# Revit family: Incepa_Zip_Acabamento Registro Base Reforma_1.2-3.4-1
name_source: partatom
category: Plumbing Fixtures
revit_build: Autodesk Revit Architecture 2014 (Build: 20131024_2115(x64)
units: mm (PartAtom-declared; Revit-internal decimal feet)

## types (1)
- Para base reforma 1/2", 3/4" e 1"
    Assembly Code = D2010
    CW Connection = No
    CWFU = 0
    Cost = 0 $
    Default Elevation = 1200 mm
    Description = Acabamento de registro para base reforma 1/2", 3/4" e 1" (B5009I9CR3), linha Incepa One - Metais Incepa
    Desenvolvido por = ofcdesk
    HW Connection = No
    HWFU = 0
    Incepa: Categoria = Lavatório
    Incepa: Cores Disponíveis = Cromado
    Incepa: Código = B5009I9CR3
    Incepa: Descrição = Acabamento de registro para base reforma 1/2", 3/4" e 1" (B5009I9CR3), linha Incepa One - Metais Incepa
    Incepa: Fabricante = Incepa
    Incepa: Linha = Incepa One
    Incepa: Norma = ABNT NBR 10283: 2008 - Requisitos e métodos de ensaio
    Incepa: Produto = Metais
    Incepa: Tipo = Acabamentos
    Incepa: Versão = Autodesk Revit MEP 2014
    Manufacturer = Incepa
    Model = B5009I9CR3
    Selo de Qualidade ofcdesk = Standard
    URL = http://www.incepa.com.br
    Vent Connection = No
    WFU = 0
    Waste Connection = No

## geometry (parser evidence)
native form markers: Blend x4, Sweep x1
no freeform markers — native parametric forms only
